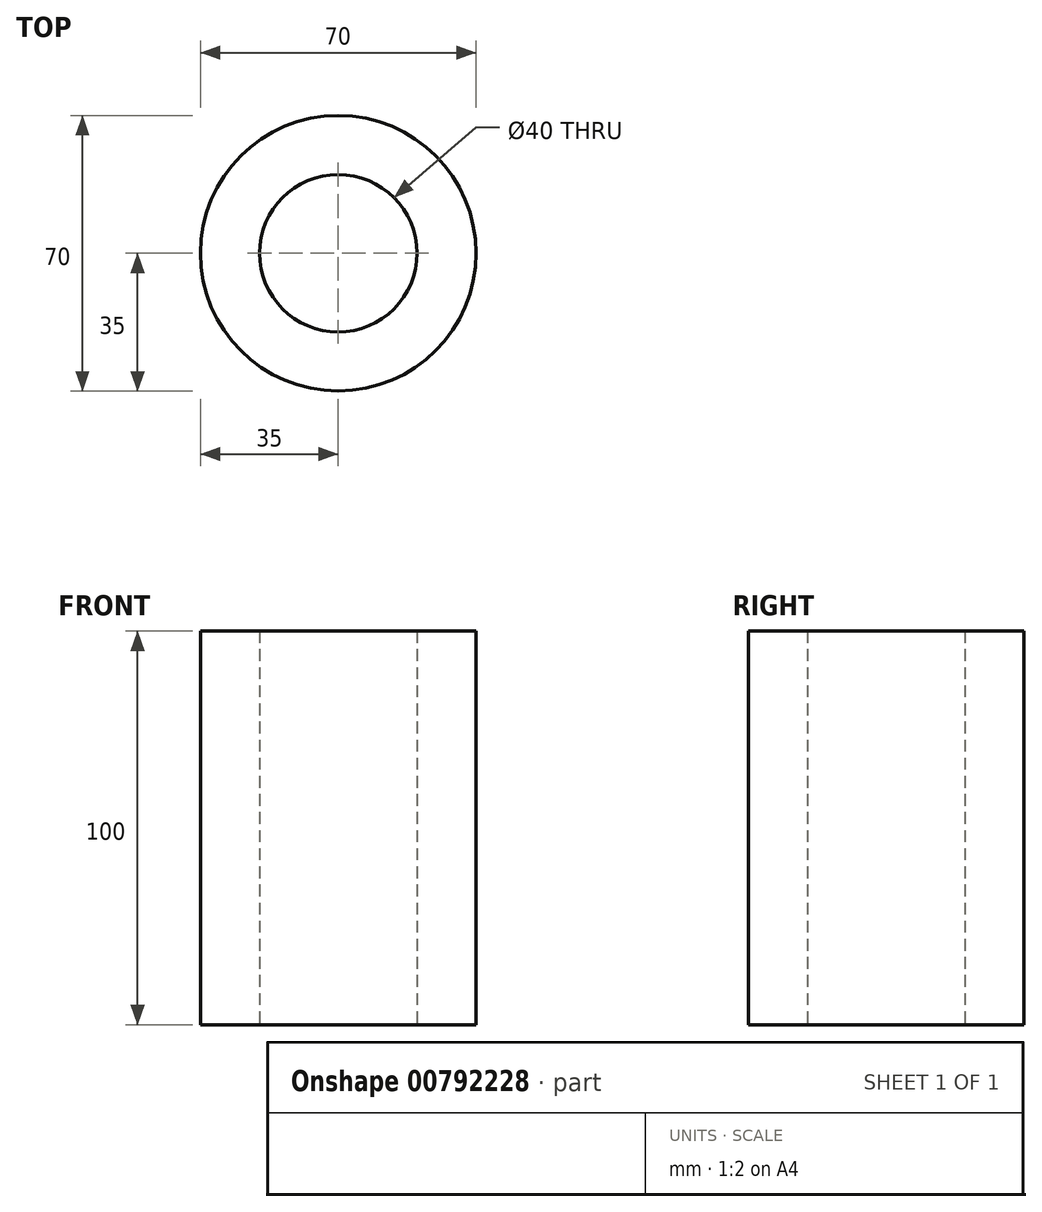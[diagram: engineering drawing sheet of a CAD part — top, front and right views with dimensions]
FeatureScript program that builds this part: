
annotation { "Feature Type Name" : "Feature", "Feature Type Description" : "" }
export const myFeature = defineFeature(function(context is Context, id is Id, definition is map)
    precondition{}
    {
        {
            var Q0;
            Q0=qCreatedBy(makeId("Top.planeOp"),FACE);
            var sketch = newSketch(context, id + "F0", { "sketchPlane" : qUnion([Q0])});
            skCircle(sketch, "E0", {"center": v(0, 0) * mm, "radius": 35 * mm});
            skCircle(sketch, "E1", {"center": v(0, 0) * mm, "radius": 20 * mm});
            skLineSegment(sketch, "E2", {"start": v(0, 0) * mm, "end": v(30.51, 17.14) * mm});
            skLineSegment(sketch, "E3", {"start": v(30.51, 17.14) * mm, "end": v(15.26, 8.57) * mm});
            skLineSegment(sketch, "E4", {"start": v(15.26, 8.57) * mm, "end": v(-38.21, -23.02) * mm});
            skSolve(sketch);
        }
        {
            var Q0;
            {var subQ0=sQuery(id+"F0.wireOp",EDGE,"E3");var subQ1=sQuery(id+"F0.wireOp",EDGE,"E0");var subQ2=makeQuery(id+"F0.imprint","INTERSECT",VERTEX,{"derivedFrom":[subQ1,subQ0]});Q0=makeQuery(id+"F0.imprint","IMPRINT",FACE,{"disambiguationData":[TD([[makeQuery(id+"F0.imprint","IMPRINT",EDGE,{"disambiguationData":[TD([[subQ2,-1.0]])],"derivedFrom":subQ1}),1.0]])]});}
            extrude(context, id + "F1", {"entities" : qUnion([Q0]), "depth" : 100 * mm, "offsetDistance" : 25 * mm});
        }
    });
